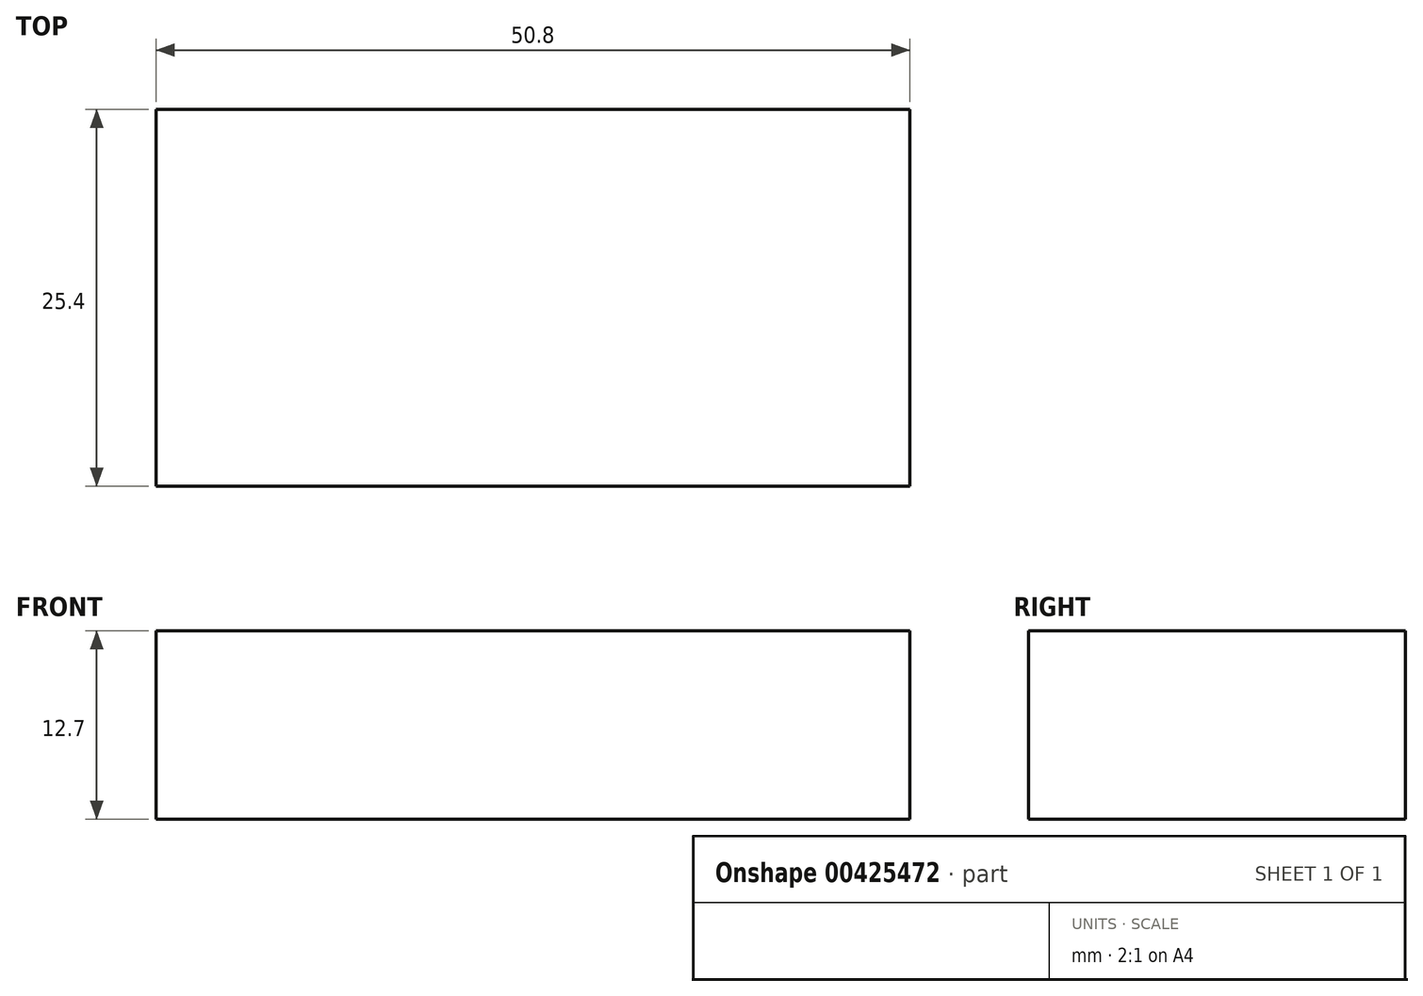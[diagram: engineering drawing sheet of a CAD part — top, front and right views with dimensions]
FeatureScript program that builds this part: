
annotation { "Feature Type Name" : "Feature", "Feature Type Description" : "" }
export const myFeature = defineFeature(function(context is Context, id is Id, definition is map)
    precondition{}
    {
        {
            var Q0;
            Q0=qCreatedBy(makeId("Top.planeOp"),FACE);
            var sketch = newSketch(context, id + "F0", { "sketchPlane" : qUnion([Q0])});
            skLineSegment(sketch, "E0.bottom", {"start": v(25.4, 12.7) * mm, "end": v(-25.4, 12.7) * mm});
            skLineSegment(sketch, "E0.top", {"start": v(25.4, -12.7) * mm, "end": v(-25.4, -12.7) * mm});
            skLineSegment(sketch, "E0.left", {"start": v(25.4, 12.7) * mm, "end": v(25.4, -12.7) * mm});
            skLineSegment(sketch, "E0.right", {"start": v(-25.4, 12.7) * mm, "end": v(-25.4, -12.7) * mm});
            skPoint(sketch, "E0.middle", {"position": v(0, 0) * mm});
            skSolve(sketch);
        }
        {
            var Q0;
            Q0=makeQuery(id+"F0.imprint","IMPRINT",FACE,{"disambiguationData":[TD([[makeQuery(id+"F0.imprint","IMPRINT",EDGE,{"derivedFrom":sQuery(id+"F0.wireOp",EDGE,"E0.bottom")}),1.0]])]});
            extrude(context, id + "F1", {"entities" : qUnion([Q0]), "depth" : 12.7 * mm});
        }
    });
